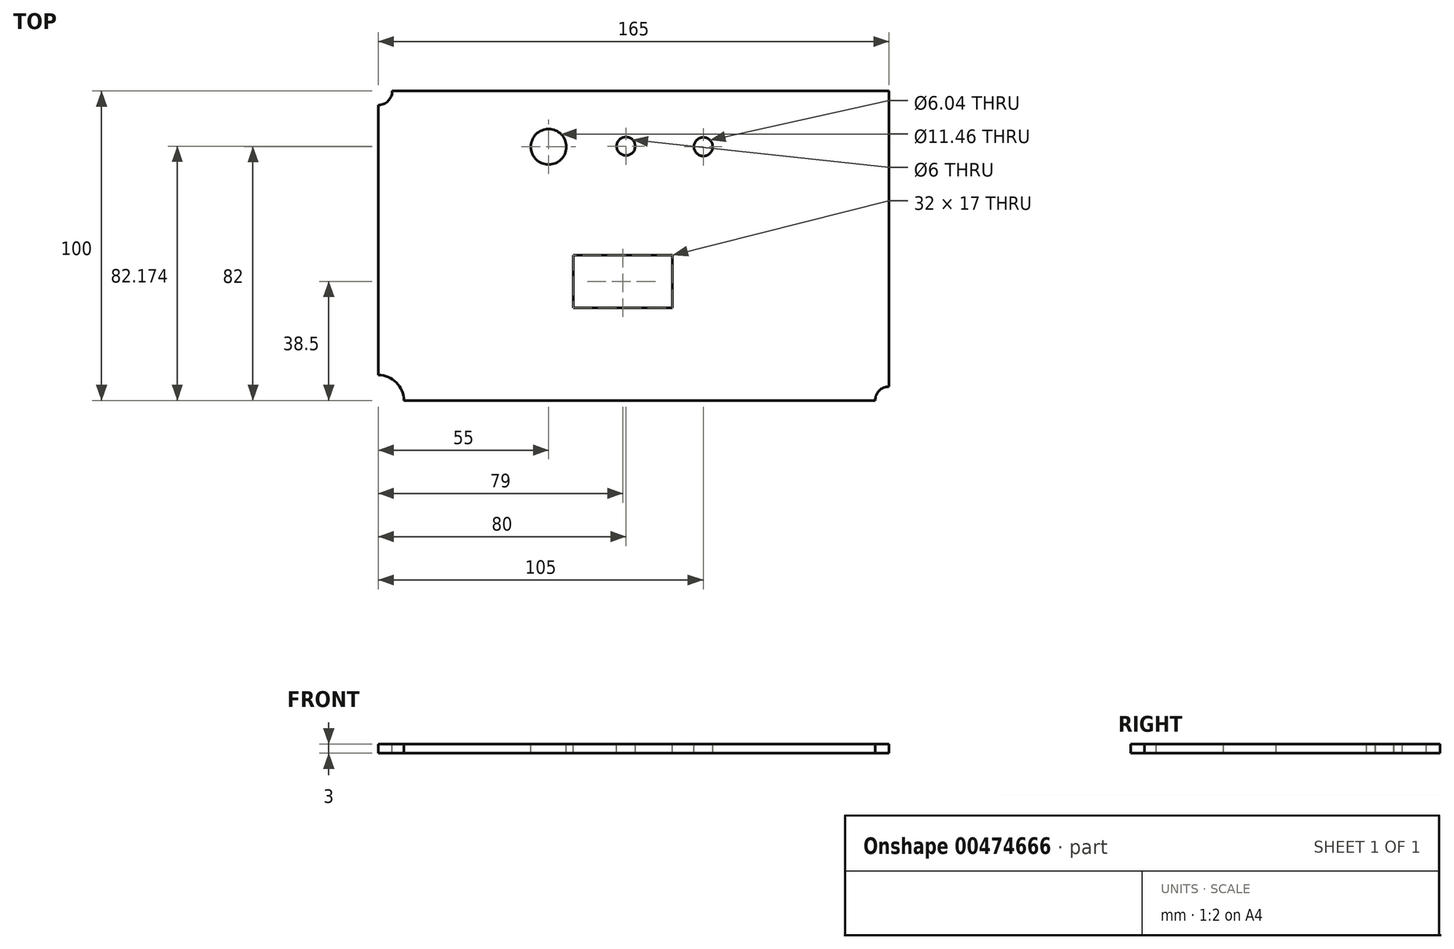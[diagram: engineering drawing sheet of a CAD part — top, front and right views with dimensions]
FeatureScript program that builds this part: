
annotation { "Feature Type Name" : "Feature", "Feature Type Description" : "" }
export const myFeature = defineFeature(function(context is Context, id is Id, definition is map)
    precondition{}
    {
        {
            var Q0;
            Q0=qCreatedBy(makeId("Top.planeOp"),FACE);
            var sketch = newSketch(context, id + "F0", { "sketchPlane" : qUnion([Q0])});
            skLineSegment(sketch, "E0.bottom", {"start": v(-82.5, 50) * mm, "end": v(82.5, 50) * mm});
            skLineSegment(sketch, "E0.top", {"start": v(-82.5, -50) * mm, "end": v(82.5, -50) * mm});
            skLineSegment(sketch, "E0.left", {"start": v(-82.5, 50) * mm, "end": v(-82.5, -50) * mm});
            skLineSegment(sketch, "E0.right", {"start": v(82.5, 50) * mm, "end": v(82.5, -50) * mm});
            skPoint(sketch, "E0.middle", {"position": v(0, 0) * mm});
            skSolve(sketch);
        }
        {
            var Q0;
            Q0 = qSketchRegion(id + "F0", true);
            extrude(context, id + "F1", {"entities" : qUnion([Q0]), "depth" : 3 * mm});
        }
        {
            var Q0;
            Q0=makeQuery(id+"F1.opExtrude","CAP_FACE",FACE,{"disambiguationData":[OSD([sQuery(id+"F0.wireOp",EDGE,"E0.bottom"),sQuery(id+"F0.wireOp",EDGE,"E0.top"),sQuery(id+"F0.wireOp",EDGE,"E0.left"),sQuery(id+"F0.wireOp",EDGE,"E0.right")])],"isStart":false});
            var sketch = newSketch(context, id + "F2", { "sketchPlane" : qUnion([Q0])});
            skCircle(sketch, "E1", {"center": v(22.5, 32) * mm, "radius": 3.02 * mm});
            skCircle(sketch, "E2", {"center": v(-2.5, 32.17) * mm, "radius": 3 * mm});
            skCircle(sketch, "E3", {"center": v(-27.5, 32) * mm, "radius": 5.73 * mm});
            skLineSegment(sketch, "E4.bottom", {"start": v(-19.5, -3) * mm, "end": v(12.5, -3) * mm});
            skLineSegment(sketch, "E4.top", {"start": v(-19.5, -20) * mm, "end": v(12.5, -20) * mm});
            skLineSegment(sketch, "E4.left", {"start": v(-19.5, -3) * mm, "end": v(-19.5, -20) * mm});
            skLineSegment(sketch, "E4.right", {"start": v(12.5, -3) * mm, "end": v(12.5, -20) * mm});
            skCircle(sketch, "E5", {"center": v(-82.5, -50) * mm, "radius": 8.23 * mm});
            skCircle(sketch, "E6", {"center": v(-82.5, 50) * mm, "radius": 4.5 * mm});
            skCircle(sketch, "E7", {"center": v(82.5, -50) * mm, "radius": 4.5 * mm});
            skSolve(sketch);
        }
        {
            var Q0;
            Q0 = qSketchRegion(id + "F2", true);
            extrude(context, id + "F3", {"entities" : qUnion([Q0]), "operationType" : NewBodyOperationType.REMOVE, "oppositeDirection" : true, "depth" : 25 * mm});
        }
    });
